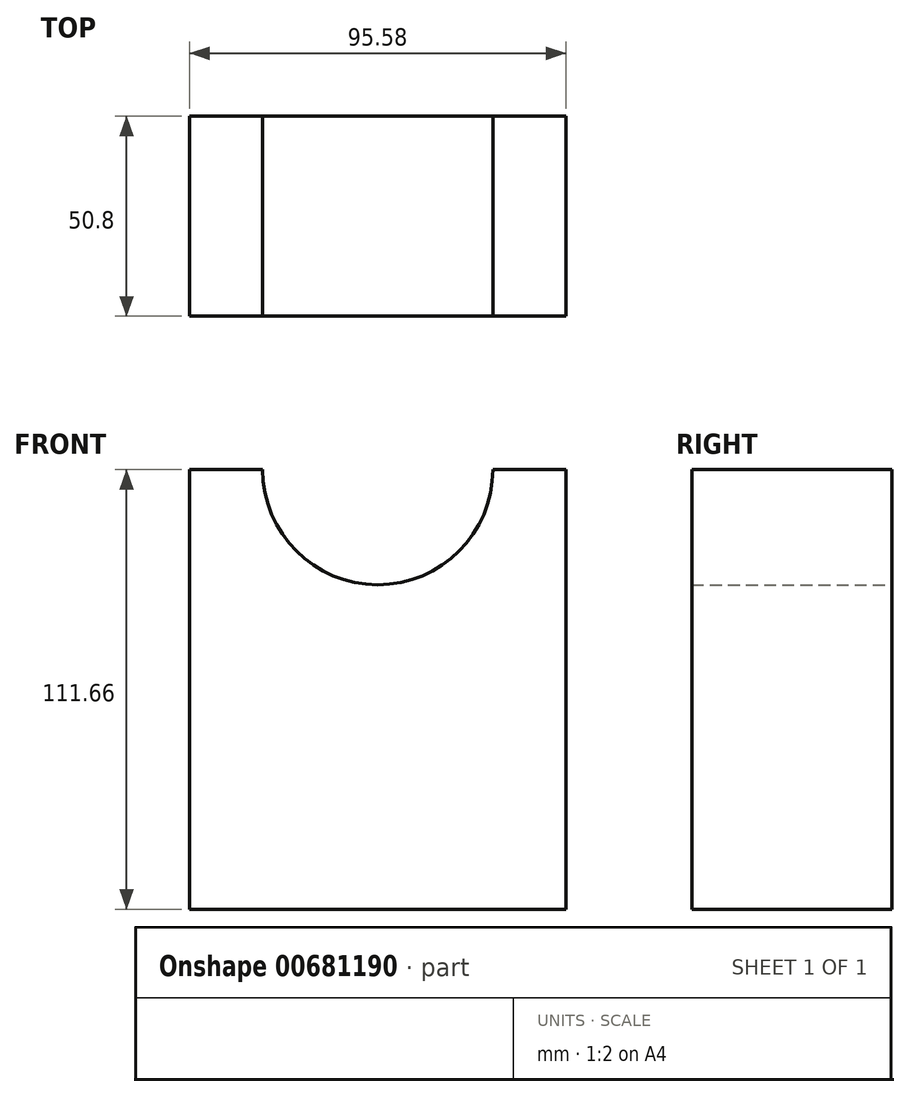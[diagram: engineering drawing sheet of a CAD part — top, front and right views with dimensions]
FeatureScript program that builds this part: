
annotation { "Feature Type Name" : "Feature", "Feature Type Description" : "" }
export const myFeature = defineFeature(function(context is Context, id is Id, definition is map)
    precondition{}
    {
        {
            var Q0;
            Q0=qCreatedBy(makeId("Front.planeOp"),FACE);
            var sketch = newSketch(context, id + "F0", { "sketchPlane" : qUnion([Q0])});
            skLineSegment(sketch, "E0.bottom", {"start": v(47.8, 55.83) * mm, "end": v(-47.8, 55.83) * mm});
            skLineSegment(sketch, "E0.top", {"start": v(47.8, -55.83) * mm, "end": v(-47.8, -55.83) * mm});
            skLineSegment(sketch, "E0.left", {"start": v(47.8, 55.83) * mm, "end": v(47.8, -55.83) * mm});
            skLineSegment(sketch, "E0.right", {"start": v(-47.8, 55.83) * mm, "end": v(-47.8, -55.83) * mm});
            skPoint(sketch, "E0.middle", {"position": v(0, 0) * mm});
            skArc(sketch, "E1", {"start": v(-47.8, 55.83) * mm, "mid": v(0, 103.63) * mm, "end": v(47.8, 55.83) * mm});
            skCircle(sketch, "E2", {"center": v(0, 55.83) * mm, "radius": 29.23 * mm});
            skSolve(sketch);
        }
        {
            var Q0;
            Q0=makeQuery(id+"F0.imprint","IMPRINT",FACE,{"disambiguationData":[TD([[makeQuery(id+"F0.imprint","IMPRINT",EDGE,{"derivedFrom":sQuery(id+"F0.wireOp",EDGE,"E0.top")}),-1.0]])]});
            var Q1;
            {var subQ0=sQuery(id+"F0.wireOp",EDGE,"E1");Q1=makeQuery(id+"F0.imprint","IMPRINT",FACE,{"disambiguationData":[TD([[makeQuery(id+"F0.imprint","IMPRINT",EDGE,{"derivedFrom":subQ0}),-1.0]])]});}
            extrude(context, id + "F1", {"entities" : qUnion([Q0, Q1]), "depth" : 50.8 * mm, "offsetDistance" : 25.4 * mm});
        }
    });
